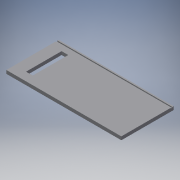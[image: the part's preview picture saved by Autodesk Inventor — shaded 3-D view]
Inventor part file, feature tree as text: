
AUTODESK INVENTOR PART (.ipt)
format: ipt  version: 2018.3 (Build 223284000, 284)  size: 118,272 bytes
history: native  units: mm
features: extrude x3, sketch x3
ambient origin geometry x8: Origin, YZ Plane, XZ Plane, XY Plane, X Axis, Y Axis, Z Axis, Center Point
bodies: Solid1 (feature_tree)
feature tree (6):
  extrude  "Extrusion1"  Depth=15.7mm
  extrude  "Extrusion3"  Depth=0.3mm
  extrude  "Extrusion5"  Depth=1.5mm TaperAngle=0.0deg
  sketch  "Sketch1"  dims[d0=34.5mm d1=15.7mm]
  sketch  "Sketch3"  dims[d2=1.0mm d3=0.0mm d8=0.3mm]
  sketch  "Sketch5"  dims[d9=0.5mm d10=40.0mm d11=0.0mm d12=0.4mm d16=2.0mm d17=0.0mm d18=2.0mm d19=10.660127mm d20=2.52mm d21=1.5mm]
